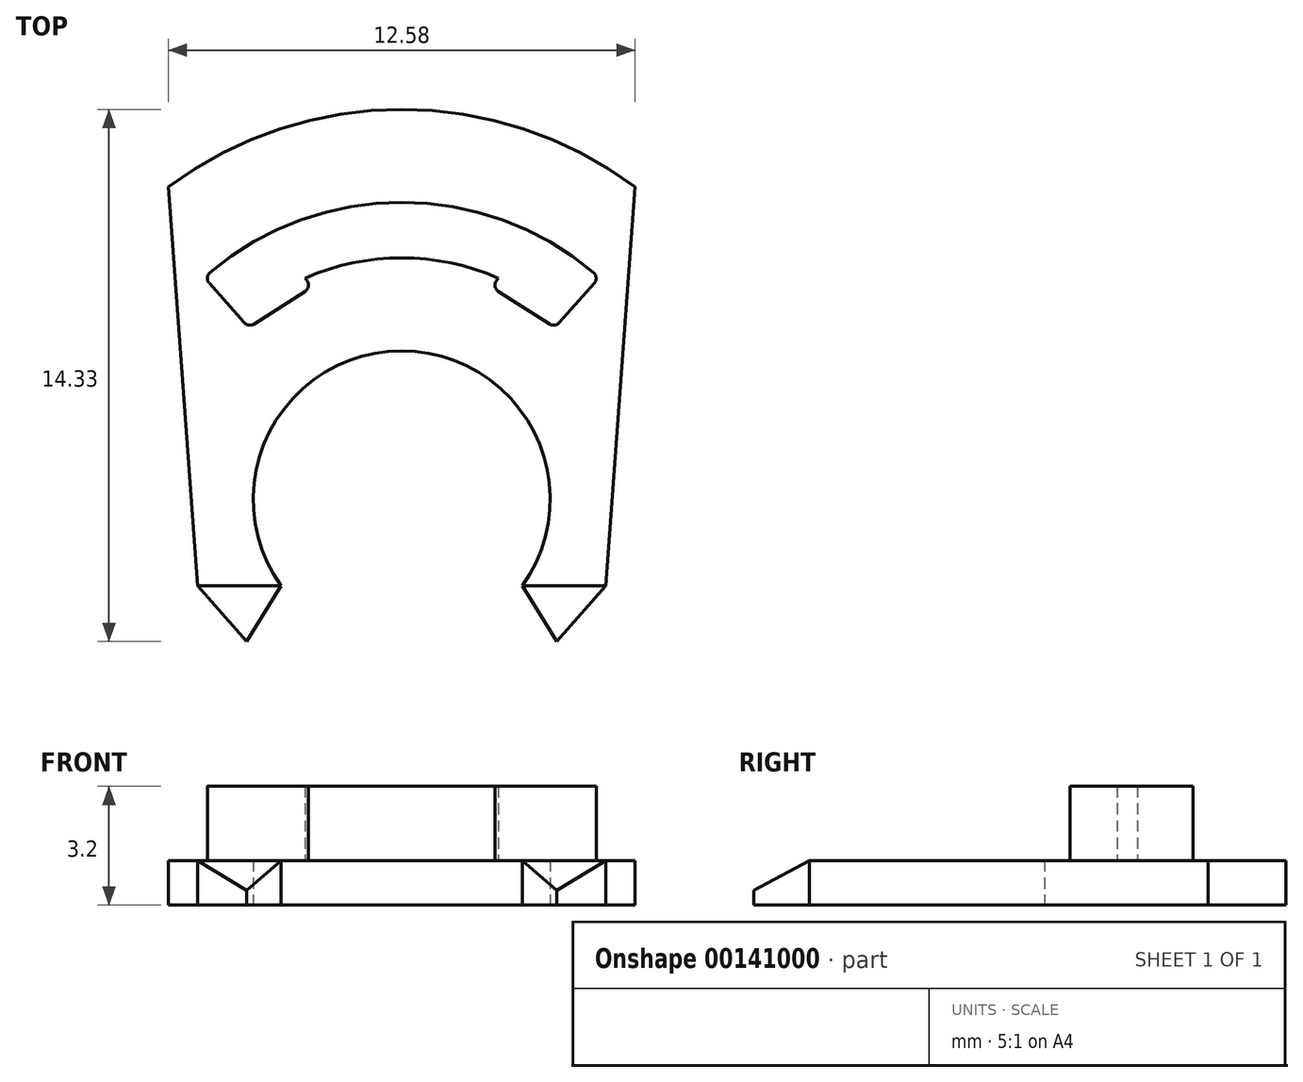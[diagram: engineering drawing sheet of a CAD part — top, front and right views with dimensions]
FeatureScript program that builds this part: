
annotation { "Feature Type Name" : "Feature", "Feature Type Description" : "" }
export const myFeature = defineFeature(function(context is Context, id is Id, definition is map)
    precondition{}
    {
        {
            var Q0;
            Q0=qCreatedBy(makeId("Top.planeOp"),FACE);
            var sketch = newSketch(context, id + "F0", { "sketchPlane" : qUnion([Q0])});
            skLineSegment(sketch, "E0", {"start": v(-7.13, -2.33) * mm, "end": v(-5.5, -2.33) * mm, "construction": true});
            skLineSegment(sketch, "E1", {"start": v(-3.25, -2.33) * mm, "end": v(3.25, -2.33) * mm, "construction": true});
            skLineSegment(sketch, "E2", {"start": v(3.25, -2.33) * mm, "end": v(5.5, -2.33) * mm, "construction": true});
            skArc(sketch, "E3", {"start": v(-7.13, -2.33) * mm, "mid": v(0, -7.5) * mm, "end": v(7.13, -2.33) * mm, "construction": true});
            skArc(sketch, "E4", {"start": v(7.13, -2.33) * mm, "mid": v(7.4, 1.22) * mm, "end": v(6, 4.5) * mm, "construction": true});
            skArc(sketch, "E5", {"start": v(3.25, -2.33) * mm, "mid": v(0, 4) * mm, "end": v(-3.25, -2.33) * mm});
            skArc(sketch, "E6", {"start": v(-3.25, -2.33) * mm, "mid": v(0, -4) * mm, "end": v(3.25, -2.33) * mm, "construction": true});
            skLineSegment(sketch, "E7", {"start": v(-6, 4.5) * mm, "end": v(6, 4.5) * mm, "construction": true});
            skArc(sketch, "E8", {"start": v(6, 4.5) * mm, "mid": v(0, 7.5) * mm, "end": v(-6, 4.5) * mm, "construction": true});
            skArc(sketch, "E9", {"start": v(-6, 4.5) * mm, "mid": v(-7.4, 1.22) * mm, "end": v(-7.13, -2.33) * mm, "construction": true});
            skLineSegment(sketch, "E10", {"start": v(-6.29, 8.41) * mm, "end": v(-5.5, -2.33) * mm});
            skLineSegment(sketch, "E11", {"start": v(6.29, 8.41) * mm, "end": v(5.5, -2.33) * mm});
            skLineSegment(sketch, "E12", {"start": v(-5.5, -2.33) * mm, "end": v(-3.25, -2.33) * mm, "construction": true});
            skLineSegment(sketch, "E13", {"start": v(5.5, -2.33) * mm, "end": v(7.13, -2.33) * mm, "construction": true});
            skLineSegment(sketch, "E14", {"start": v(-5.5, -2.33) * mm, "end": v(-4.18, -3.83) * mm});
            skLineSegment(sketch, "E15", {"start": v(-4.18, -3.83) * mm, "end": v(-3.25, -2.33) * mm});
            skLineSegment(sketch, "E16", {"start": v(3.25, -2.33) * mm, "end": v(4.18, -3.83) * mm});
            skLineSegment(sketch, "E17", {"start": v(4.18, -3.83) * mm, "end": v(5.5, -2.33) * mm});
            skArc(sketch, "E18", {"start": v(-6.29, 8.41) * mm, "mid": v(0, 10.5) * mm, "end": v(6.29, 8.41) * mm});
            skPoint(sketch, "E19", {"position": v(0, 10.5) * mm});
            skPoint(sketch, "E20", {"position": v(0, 7.5) * mm});
            skSolve(sketch);
        }
        {
            var Q0;
            Q0 = qSketchRegion(id + "F0", true);
            extrude(context, id + "F1", {"entities" : qUnion([Q0]), "depth" : 1.2 * mm});
        }
        {
            var Q0;
            Q0=qCreatedBy(makeId("Right.planeOp"),FACE);
            var sketch = newSketch(context, id + "F2", { "sketchPlane" : qUnion([Q0])});
            skPoint(sketch, "E21.0", {"position": v(-2.33, 1.2) * mm});
            skLineSegment(sketch, "E22", {"start": v(-2.33, 1.2) * mm, "end": v(-3.83, 0.4) * mm});
            skLineSegment(sketch, "E23", {"start": v(-3.83, 0.4) * mm, "end": v(-3.83, 1.2) * mm});
            skLineSegment(sketch, "E24", {"start": v(-2.33, 1.2) * mm, "end": v(-3.83, 1.2) * mm});
            skSolve(sketch);
        }
        {
            var Q0;
            Q0 = qSketchRegion(id + "F2", true);
            extrude(context, id + "F3", {"entities" : qUnion([Q0]), "operationType" : NewBodyOperationType.REMOVE, "endBound" : BoundingType.SYMMETRIC, "oppositeDirection" : true, "depth" : 25 * mm});
        }
        {
            var Q0;
            Q0=makeQuery(id+"F1.opExtrude","CAP_FACE",FACE,{"disambiguationData":[OSD([sQuery(id+"F0.wireOp",EDGE,"E5"),sQuery(id+"F0.wireOp",EDGE,"E10"),sQuery(id+"F0.wireOp",EDGE,"E11"),sQuery(id+"F0.wireOp",EDGE,"E14"),sQuery(id+"F0.wireOp",EDGE,"E15"),sQuery(id+"F0.wireOp",EDGE,"E16"),sQuery(id+"F0.wireOp",EDGE,"E17"),sQuery(id+"F0.wireOp",EDGE,"E18")])],"isStart":false});
            var sketch = newSketch(context, id + "F4", { "sketchPlane" : qUnion([Q0])});
            skArc(sketch, "E25.0", {"start": v(0, 8) * mm, "mid": v(-2.75, 7.51) * mm, "end": v(-5.17, 6.1) * mm});
            skArc(sketch, "E26.0", {"start": v(0, 6.5) * mm, "mid": v(-1.33, 6.36) * mm, "end": v(-2.6, 5.96) * mm});
            skPoint(sketch, "E27", {"position": v(0, 8) * mm});
            skPoint(sketch, "E28", {"position": v(0, 6.5) * mm});
            skLineSegment(sketch, "E29", {"start": v(-5.32, 5.97) * mm, "end": v(-5.74, 5.6) * mm, "construction": true});
            skLineSegment(sketch, "E30", {"start": v(-5.19, 5.82) * mm, "end": v(-4.32, 4.85) * mm});
            skLineSegment(sketch, "E31", {"start": v(-4.32, 4.85) * mm, "end": v(-4.24, 4.76) * mm});
            skLineSegment(sketch, "E32", {"start": v(-3.98, 4.72) * mm, "end": v(-2.6, 5.6) * mm});
            skLineSegment(sketch, "E33", {"start": v(-2.54, 5.87) * mm, "end": v(-2.6, 5.96) * mm});
            skLineSegment(sketch, "E34", {"start": v(0, 8) * mm, "end": v(0, 6.5) * mm, "construction": true});
            skPoint(sketch, "E35.start.orphan", {"position": v(4.68, 6.5) * mm});
            skPoint(sketch, "E36.visualSharp", {"position": v(-5.32, 5.97) * mm});
            skArc(sketch, "E36.filletArc", {"start": v(-5.17, 6.1) * mm, "mid": v(-5.24, 5.97) * mm, "end": v(-5.19, 5.82) * mm});
            skPoint(sketch, "E37.visualSharp", {"position": v(-4.13, 4.63) * mm});
            skArc(sketch, "E37.filletArc", {"start": v(-4.24, 4.76) * mm, "mid": v(-4.12, 4.7) * mm, "end": v(-3.98, 4.72) * mm});
            skPoint(sketch, "E38.visualSharp", {"position": v(-2.44, 5.7) * mm});
            skArc(sketch, "E38.filletArc", {"start": v(-2.6, 5.6) * mm, "mid": v(-2.52, 5.72) * mm, "end": v(-2.54, 5.87) * mm});
            skLineSegment(sketch, "E39.MirrorCS", {"start": v(4.32, 4.85) * mm, "end": v(4.24, 4.76) * mm});
            skArc(sketch, "E40.MirrorCS", {"start": v(4.24, 4.76) * mm, "mid": v(4.12, 4.7) * mm, "end": v(3.98, 4.72) * mm});
            skLineSegment(sketch, "E41.MirrorCS", {"start": v(3.98, 4.72) * mm, "end": v(2.6, 5.6) * mm});
            skPoint(sketch, "E42.MirrorP", {"position": v(4.13, 4.63) * mm});
            skLineSegment(sketch, "E43.MirrorCS", {"start": v(5.19, 5.82) * mm, "end": v(4.32, 4.85) * mm});
            skArc(sketch, "E44.MirrorCS", {"start": v(0, 8) * mm, "mid": v(2.75, 7.51) * mm, "end": v(5.17, 6.1) * mm});
            skLineSegment(sketch, "E45.MirrorCS", {"start": v(2.54, 5.87) * mm, "end": v(2.6, 5.96) * mm});
            skArc(sketch, "E46.MirrorCS", {"start": v(2.6, 5.6) * mm, "mid": v(2.52, 5.72) * mm, "end": v(2.54, 5.87) * mm});
            skArc(sketch, "E47.MirrorCS", {"start": v(5.17, 6.1) * mm, "mid": v(5.24, 5.97) * mm, "end": v(5.19, 5.82) * mm});
            skArc(sketch, "E48.MirrorCS", {"start": v(0, 6.5) * mm, "mid": v(1.33, 6.36) * mm, "end": v(2.6, 5.96) * mm});
            skPoint(sketch, "E49.MirrorP", {"position": v(5.32, 5.97) * mm});
            skPoint(sketch, "E50.MirrorP", {"position": v(2.44, 5.7) * mm});
            skSolve(sketch);
        }
        {
            var Q0;
            Q0 = qSketchRegion(id + "F4", true);
            extrude(context, id + "F5", {"entities" : qUnion([Q0]), "operationType" : NewBodyOperationType.ADD, "depth" : 2 * mm});
        }
    });
